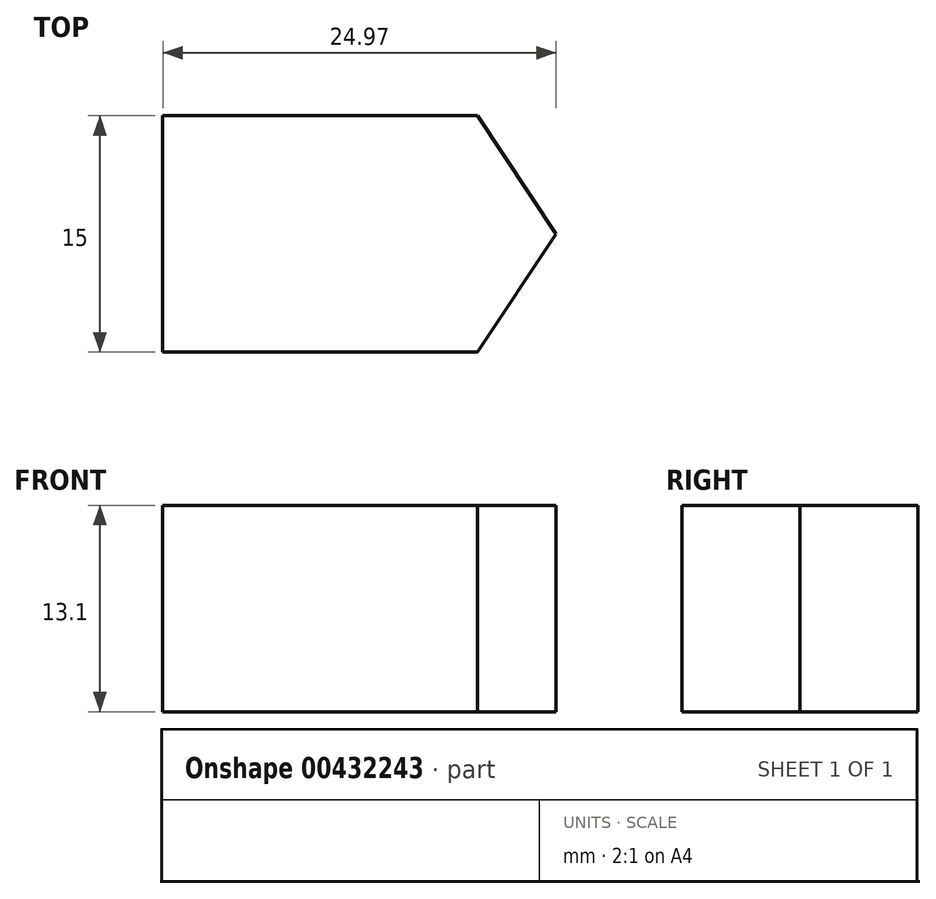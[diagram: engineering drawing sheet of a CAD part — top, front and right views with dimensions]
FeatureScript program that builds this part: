
annotation { "Feature Type Name" : "Feature", "Feature Type Description" : "" }
export const myFeature = defineFeature(function(context is Context, id is Id, definition is map)
    precondition{}
    {
        {
            var Q0;
            Q0=qCreatedBy(makeId("Top.planeOp"),FACE);
            var sketch = newSketch(context, id + "F0", { "sketchPlane" : qUnion([Q0])});
            skLineSegment(sketch, "E0.bottom", {"start": v(-13.06, 7.5) * mm, "end": v(6.94, 7.5) * mm});
            skLineSegment(sketch, "E0.top", {"start": v(-13.06, -7.5) * mm, "end": v(6.94, -7.5) * mm});
            skLineSegment(sketch, "E0.left", {"start": v(-13.06, 7.5) * mm, "end": v(-13.06, -7.5) * mm});
            skLineSegment(sketch, "E0.right", {"start": v(6.94, 7.5) * mm, "end": v(6.94, -7.5) * mm});
            skLineSegment(sketch, "E1", {"start": v(6.94, 7.5) * mm, "end": v(11.91, 0) * mm});
            skLineSegment(sketch, "E2", {"start": v(6.94, -7.5) * mm, "end": v(11.91, 0) * mm});
            skSolve(sketch);
        }
        {
            var Q0;
            Q0 = qSketchRegion(id + "F0", true);
            extrude(context, id + "F1", {"entities" : qUnion([Q0]), "depth" : 13.1 * mm});
        }
    });
